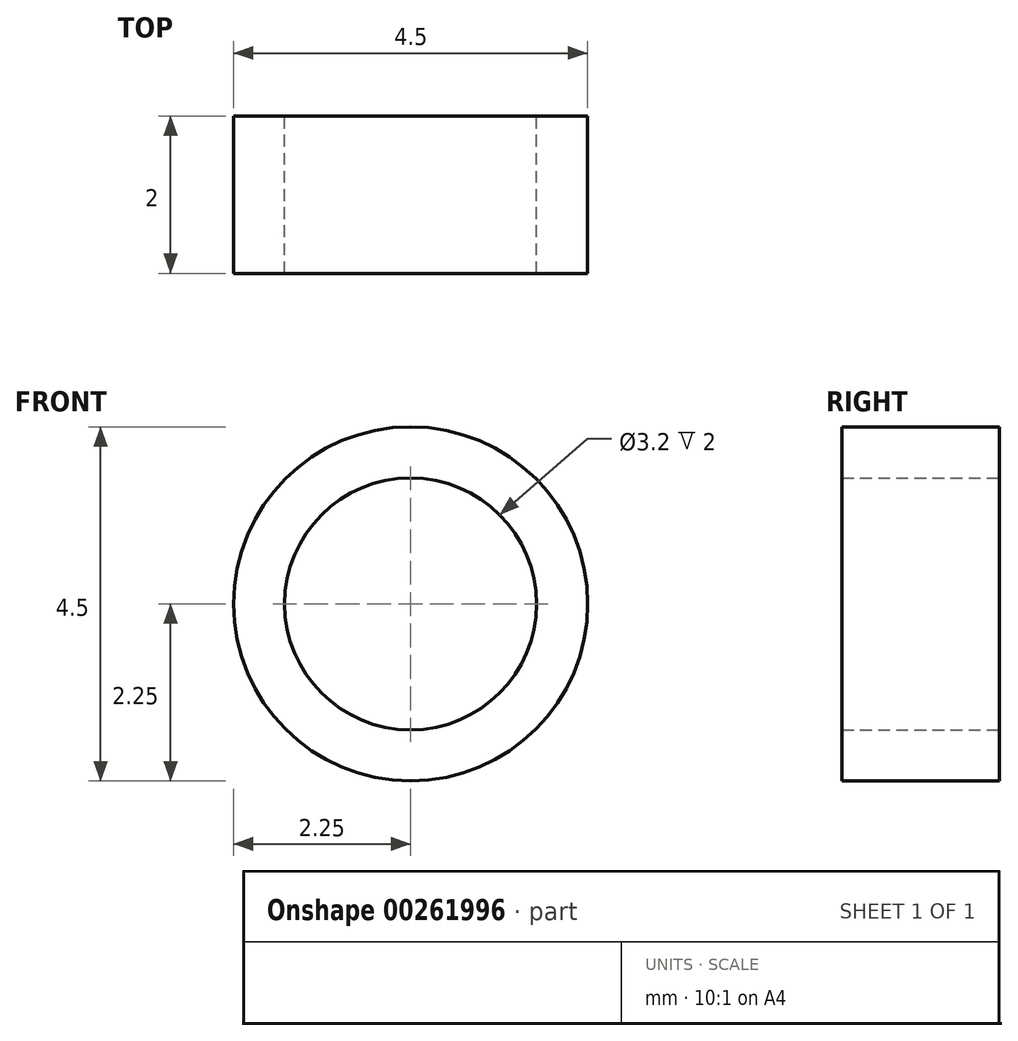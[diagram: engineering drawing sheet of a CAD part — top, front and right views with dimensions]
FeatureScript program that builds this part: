
annotation { "Feature Type Name" : "Feature", "Feature Type Description" : "" }
export const myFeature = defineFeature(function(context is Context, id is Id, definition is map)
    precondition{}
    {
        {
            assignVariable(context, id + "F0", {"name" : "Hieght", "anyValue" : 2});
        }
        {
            var Q0;
            Q0=qCreatedBy(makeId("Front.planeOp"),FACE);
            var sketch = newSketch(context, id + "F1", { "sketchPlane" : qUnion([Q0])});
            skCircle(sketch, "E0", {"center": v(0, 0) * mm, "radius": 1.6 * mm});
            skCircle(sketch, "E1", {"center": v(0, 0) * mm, "radius": 2.25 * mm});
            skSolve(sketch);
        }
        {
            var Q0;
            Q0=makeQuery(id+"F1.imprint","IMPRINT",FACE,{"disambiguationData":[TD([[makeQuery(id+"F1.imprint","IMPRINT",EDGE,{"derivedFrom":sQuery(id+"F1.wireOp",EDGE,"E0")}),-1.0]])]});
            extrude(context, id + "F2", {"entities" : qUnion([Q0]), "depth" : getVariable(context, 'Hieght') * mm});
        }
    });
